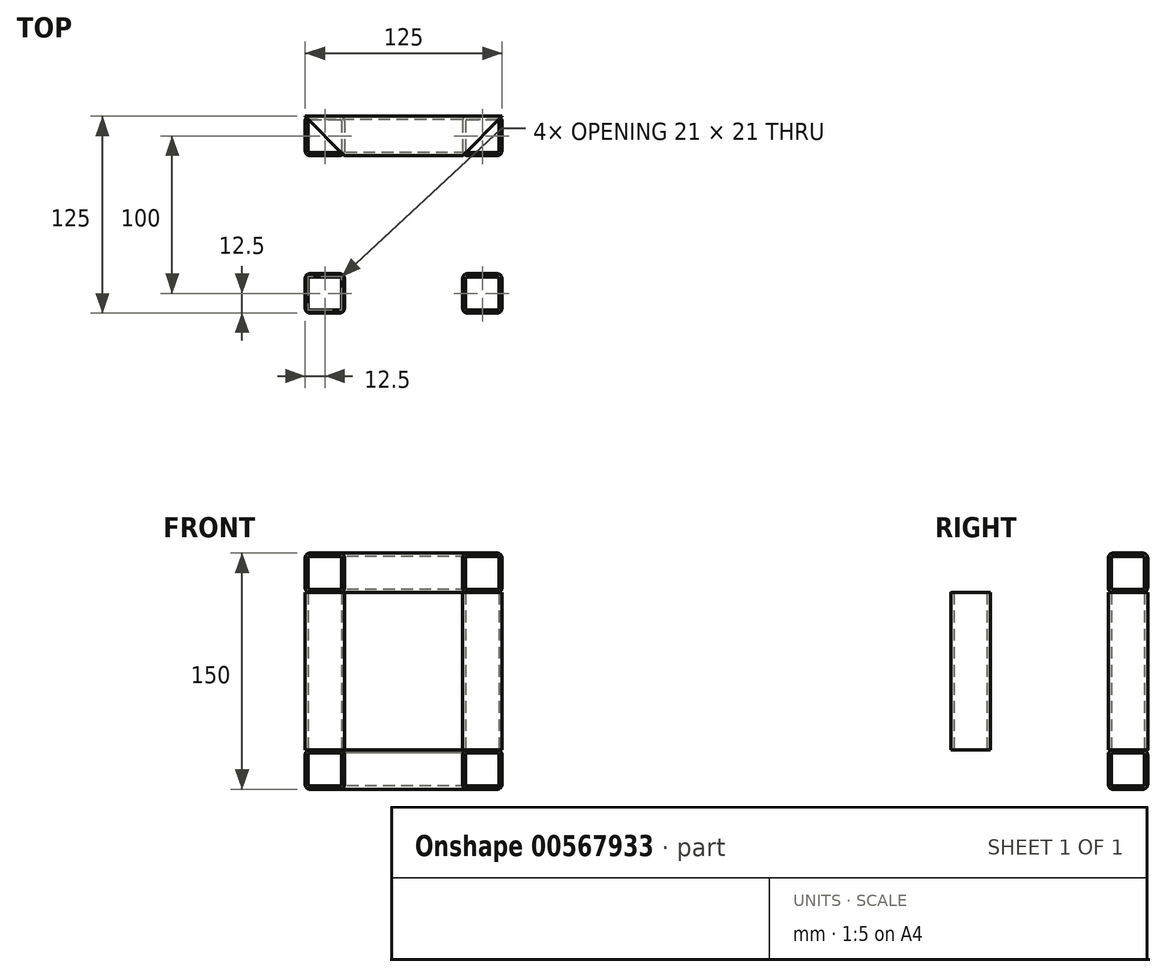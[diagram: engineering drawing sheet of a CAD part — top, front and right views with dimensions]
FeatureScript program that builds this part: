
annotation { "Feature Type Name" : "Feature", "Feature Type Description" : "" }
export const myFeature = defineFeature(function(context is Context, id is Id, definition is map)
    precondition{}
    {
        {
            var Q0;
            Q0=qCreatedBy(makeId("Top.planeOp"),FACE);
            var sketch = newSketch(context, id + "F0", { "sketchPlane" : qUnion([Q0])});
            skLineSegment(sketch, "E0.bottom", {"start": v(-59.5, 62.5) * mm, "end": v(-40.5, 62.5) * mm});
            skLineSegment(sketch, "E0.top", {"start": v(-59.5, 37.5) * mm, "end": v(-40.5, 37.5) * mm});
            skLineSegment(sketch, "E0.left", {"start": v(-62.5, 59.5) * mm, "end": v(-62.5, 40.5) * mm});
            skLineSegment(sketch, "E0.right", {"start": v(-37.5, 59.5) * mm, "end": v(-37.5, 40.5) * mm});
            skPoint(sketch, "E1.visualSharp", {"position": v(-62.5, 62.5) * mm});
            skArc(sketch, "E1.filletArc", {"start": v(-59.5, 62.5) * mm, "mid": v(-61.62, 61.62) * mm, "end": v(-62.5, 59.5) * mm});
            skPoint(sketch, "E2.visualSharp", {"position": v(-37.5, 62.5) * mm});
            skArc(sketch, "E2.filletArc", {"start": v(-37.5, 59.5) * mm, "mid": v(-38.38, 61.62) * mm, "end": v(-40.5, 62.5) * mm});
            skPoint(sketch, "E3.visualSharp", {"position": v(-37.5, 37.5) * mm});
            skArc(sketch, "E3.filletArc", {"start": v(-40.5, 37.5) * mm, "mid": v(-38.38, 38.38) * mm, "end": v(-37.5, 40.5) * mm});
            skPoint(sketch, "E4.visualSharp", {"position": v(-62.5, 37.5) * mm});
            skArc(sketch, "E4.filletArc", {"start": v(-62.5, 40.5) * mm, "mid": v(-61.62, 38.38) * mm, "end": v(-59.5, 37.5) * mm});
            skLineSegment(sketch, "E5.0", {"start": v(-59.5, 60.5) * mm, "end": v(-40.5, 60.5) * mm});
            skArc(sketch, "E5.1", {"start": v(-39.5, 59.5) * mm, "mid": v(-39.8, 60.2) * mm, "end": v(-40.5, 60.5) * mm});
            skArc(sketch, "E5.2", {"start": v(-59.5, 60.5) * mm, "mid": v(-60.2, 60.2) * mm, "end": v(-60.5, 59.5) * mm});
            skLineSegment(sketch, "E5.3", {"start": v(-39.5, 59.5) * mm, "end": v(-39.5, 40.5) * mm});
            skLineSegment(sketch, "E5.4", {"start": v(-60.5, 59.5) * mm, "end": v(-60.5, 40.5) * mm});
            skArc(sketch, "E5.5", {"start": v(-60.5, 40.5) * mm, "mid": v(-60.2, 39.8) * mm, "end": v(-59.5, 39.5) * mm});
            skLineSegment(sketch, "E5.6", {"start": v(-59.5, 39.5) * mm, "end": v(-40.5, 39.5) * mm});
            skArc(sketch, "E5.7", {"start": v(-40.5, 39.5) * mm, "mid": v(-39.8, 39.8) * mm, "end": v(-39.5, 40.5) * mm});
            skSolve(sketch);
        }
        {
            var Q0;
            Q0 = qSketchRegion(id + "F0", true);
            extrude(context, id + "F1", {"entities" : qUnion([Q0]), "depth" : 100 * mm, "offsetDistance" : 25 * mm});
        }
        {
            var Q0;
            Q0=makeQuery(id+"F1.opExtrude","SWEPT_BODY",BODY,{"disambiguationData":[OSD([sQuery(id+"F0.wireOp",EDGE,"E0.bottom"),sQuery(id+"F0.wireOp",EDGE,"E0.top"),sQuery(id+"F0.wireOp",EDGE,"E0.left"),sQuery(id+"F0.wireOp",EDGE,"E0.right"),sQuery(id+"F0.wireOp",EDGE,"E1.filletArc"),sQuery(id+"F0.wireOp",EDGE,"E2.filletArc"),sQuery(id+"F0.wireOp",EDGE,"E3.filletArc"),sQuery(id+"F0.wireOp",EDGE,"E4.filletArc"),sQuery(id+"F0.wireOp",EDGE,"E5.0"),sQuery(id+"F0.wireOp",EDGE,"E5.1"),sQuery(id+"F0.wireOp",EDGE,"E5.2"),sQuery(id+"F0.wireOp",EDGE,"E5.3"),sQuery(id+"F0.wireOp",EDGE,"E5.4"),sQuery(id+"F0.wireOp",EDGE,"E5.5"),sQuery(id+"F0.wireOp",EDGE,"E5.6"),sQuery(id+"F0.wireOp",EDGE,"E5.7")])]});
            transform(context, id + "F2", {"entities" : qUnion([Q0]), "transformType" : TransformType.TRANSLATION_3D, "dx" : 100 * mm, "dy" : 0 * mm, "dz" : 0 * mm, "makeCopy" : true});
        }
        {
            var Q0;
            Q0=makeQuery(id+"F1.opExtrude","SWEPT_BODY",BODY,{"disambiguationData":[OSD([sQuery(id+"F0.wireOp",EDGE,"E0.bottom"),sQuery(id+"F0.wireOp",EDGE,"E0.top"),sQuery(id+"F0.wireOp",EDGE,"E0.left"),sQuery(id+"F0.wireOp",EDGE,"E0.right"),sQuery(id+"F0.wireOp",EDGE,"E1.filletArc"),sQuery(id+"F0.wireOp",EDGE,"E2.filletArc"),sQuery(id+"F0.wireOp",EDGE,"E3.filletArc"),sQuery(id+"F0.wireOp",EDGE,"E4.filletArc"),sQuery(id+"F0.wireOp",EDGE,"E5.0"),sQuery(id+"F0.wireOp",EDGE,"E5.1"),sQuery(id+"F0.wireOp",EDGE,"E5.2"),sQuery(id+"F0.wireOp",EDGE,"E5.3"),sQuery(id+"F0.wireOp",EDGE,"E5.4"),sQuery(id+"F0.wireOp",EDGE,"E5.5"),sQuery(id+"F0.wireOp",EDGE,"E5.6"),sQuery(id+"F0.wireOp",EDGE,"E5.7")])]});
            transform(context, id + "F3", {"entities" : qUnion([Q0]), "transformType" : TransformType.TRANSLATION_3D, "dx" : 0 * mm, "dy" : -100 * mm, "dz" : 0 * mm, "makeCopy" : true});
        }
        {
            var Q0;
            Q0=makeQuery(id+"F3.opPattern","COPY",BODY,{"derivedFrom":makeQuery(id+"F1.opExtrude","SWEPT_BODY",BODY,{"disambiguationData":[OSD([sQuery(id+"F0.wireOp",EDGE,"E0.bottom"),sQuery(id+"F0.wireOp",EDGE,"E0.top"),sQuery(id+"F0.wireOp",EDGE,"E0.left"),sQuery(id+"F0.wireOp",EDGE,"E0.right"),sQuery(id+"F0.wireOp",EDGE,"E1.filletArc"),sQuery(id+"F0.wireOp",EDGE,"E2.filletArc"),sQuery(id+"F0.wireOp",EDGE,"E3.filletArc"),sQuery(id+"F0.wireOp",EDGE,"E4.filletArc"),sQuery(id+"F0.wireOp",EDGE,"E5.0"),sQuery(id+"F0.wireOp",EDGE,"E5.1"),sQuery(id+"F0.wireOp",EDGE,"E5.2"),sQuery(id+"F0.wireOp",EDGE,"E5.3"),sQuery(id+"F0.wireOp",EDGE,"E5.4"),sQuery(id+"F0.wireOp",EDGE,"E5.5"),sQuery(id+"F0.wireOp",EDGE,"E5.6"),sQuery(id+"F0.wireOp",EDGE,"E5.7")])]}),"instanceName":"1"});
            transform(context, id + "F4", {"entities" : qUnion([Q0]), "transformType" : TransformType.TRANSLATION_3D, "dx" : 100 * mm, "dy" : 0 * mm, "dz" : 0 * mm, "makeCopy" : true});
        }
        {
            var Q0;
            Q0=qCreatedBy(makeId("Right.planeOp"),FACE);
            var sketch = newSketch(context, id + "F5", { "sketchPlane" : qUnion([Q0])});
            skLineSegment(sketch, "E6.bottom", {"start": v(40.5, 125) * mm, "end": v(59.5, 125) * mm});
            skLineSegment(sketch, "E6.top", {"start": v(40.5, 100) * mm, "end": v(59.5, 100) * mm});
            skLineSegment(sketch, "E6.left", {"start": v(37.5, 122) * mm, "end": v(37.5, 103) * mm});
            skLineSegment(sketch, "E6.right", {"start": v(62.5, 122) * mm, "end": v(62.5, 103) * mm});
            skPoint(sketch, "E6.middle", {"position": v(50, 112.5) * mm});
            skPoint(sketch, "E7.visualSharp", {"position": v(62.5, 125) * mm});
            skArc(sketch, "E7.filletArc", {"start": v(62.5, 122) * mm, "mid": v(61.62, 124.12) * mm, "end": v(59.5, 125) * mm});
            skPoint(sketch, "E8.visualSharp", {"position": v(37.5, 125) * mm});
            skArc(sketch, "E8.filletArc", {"start": v(40.5, 125) * mm, "mid": v(38.38, 124.12) * mm, "end": v(37.5, 122) * mm});
            skPoint(sketch, "E9.visualSharp", {"position": v(37.5, 100) * mm});
            skArc(sketch, "E9.filletArc", {"start": v(37.5, 103) * mm, "mid": v(38.38, 100.88) * mm, "end": v(40.5, 100) * mm});
            skPoint(sketch, "E10.visualSharp", {"position": v(62.5, 100) * mm});
            skArc(sketch, "E10.filletArc", {"start": v(59.5, 100) * mm, "mid": v(61.62, 100.88) * mm, "end": v(62.5, 103) * mm});
            skArc(sketch, "E11.0", {"start": v(39.5, 103) * mm, "mid": v(39.8, 102.3) * mm, "end": v(40.5, 102) * mm});
            skLineSegment(sketch, "E11.1", {"start": v(39.5, 122) * mm, "end": v(39.5, 103) * mm});
            skLineSegment(sketch, "E11.2", {"start": v(40.5, 102) * mm, "end": v(59.5, 102) * mm});
            skArc(sketch, "E11.3", {"start": v(40.5, 123) * mm, "mid": v(39.8, 122.7) * mm, "end": v(39.5, 122) * mm});
            skArc(sketch, "E11.4", {"start": v(59.5, 102) * mm, "mid": v(60.2, 102.3) * mm, "end": v(60.5, 103) * mm});
            skLineSegment(sketch, "E11.5", {"start": v(60.5, 122) * mm, "end": v(60.5, 103) * mm});
            skArc(sketch, "E11.6", {"start": v(60.5, 122) * mm, "mid": v(60.2, 122.7) * mm, "end": v(59.5, 123) * mm});
            skLineSegment(sketch, "E11.7", {"start": v(40.5, 123) * mm, "end": v(59.5, 123) * mm});
            skSolve(sketch);
        }
        {
            var Q0;
            Q0 = qSketchRegion(id + "F5", true);
            extrude(context, id + "F6", {"entities" : qUnion([Q0]), "endBound" : BoundingType.SYMMETRIC, "depth" : 150 * mm, "offsetDistance" : 25 * mm});
        }
        {
            var Q0;
            Q0=makeQuery(id+"F6.opExtrude","SWEPT_FACE",FACE,{"disambiguationData":[OSD([sQuery(id+"F5.wireOp",EDGE,"E6.bottom")])]});
            var sketch = newSketch(context, id + "F7", { "sketchPlane" : qUnion([Q0])});
            skLineSegment(sketch, "E12", {"start": v(0, 0) * mm, "end": v(-102.25, 102.25) * mm});
            skLineSegment(sketch, "E13", {"start": v(-102.25, 102.25) * mm, "end": v(-102.25, 0) * mm});
            skLineSegment(sketch, "E14", {"start": v(-102.25, 0) * mm, "end": v(0, 0) * mm});
            skSolve(sketch);
        }
        {
            var Q0;
            Q0 = qSketchRegion(id + "F7", true);
            extrude(context, id + "F8", {"entities" : qUnion([Q0]), "operationType" : NewBodyOperationType.REMOVE, "oppositeDirection" : true, "depth" : 25 * mm, "offsetDistance" : 25 * mm});
        }
        {
            var Q0;
            Q0=makeQuery(id+"F6.opExtrude","SWEPT_FACE",FACE,{"disambiguationData":[OSD([sQuery(id+"F5.wireOp",EDGE,"E6.bottom")])]});
            var sketch = newSketch(context, id + "F9", { "sketchPlane" : qUnion([Q0])});
            skLineSegment(sketch, "E15", {"start": v(0, 0) * mm, "end": v(99.52, 99.52) * mm});
            skLineSegment(sketch, "E16", {"start": v(99.52, 99.52) * mm, "end": v(99.52, 0) * mm});
            skLineSegment(sketch, "E17", {"start": v(99.52, 0) * mm, "end": v(0, 0) * mm});
            skSolve(sketch);
        }
        {
            var Q0;
            Q0 = qSketchRegion(id + "F9", true);
            extrude(context, id + "F10", {"entities" : qUnion([Q0]), "operationType" : NewBodyOperationType.REMOVE, "oppositeDirection" : true, "depth" : 25 * mm, "offsetDistance" : 25 * mm});
        }
        {
            var Q0;
            Q0=makeQuery(id+"F6.opExtrude","SWEPT_BODY",BODY,{"disambiguationData":[OSD([sQuery(id+"F5.wireOp",EDGE,"E6.bottom"),sQuery(id+"F5.wireOp",EDGE,"E6.top"),sQuery(id+"F5.wireOp",EDGE,"E6.left"),sQuery(id+"F5.wireOp",EDGE,"E6.right"),sQuery(id+"F5.wireOp",EDGE,"E7.filletArc"),sQuery(id+"F5.wireOp",EDGE,"E8.filletArc"),sQuery(id+"F5.wireOp",EDGE,"E9.filletArc"),sQuery(id+"F5.wireOp",EDGE,"E10.filletArc"),sQuery(id+"F5.wireOp",EDGE,"E11.0"),sQuery(id+"F5.wireOp",EDGE,"E11.1"),sQuery(id+"F5.wireOp",EDGE,"E11.2"),sQuery(id+"F5.wireOp",EDGE,"E11.3"),sQuery(id+"F5.wireOp",EDGE,"E11.4"),sQuery(id+"F5.wireOp",EDGE,"E11.5"),sQuery(id+"F5.wireOp",EDGE,"E11.6"),sQuery(id+"F5.wireOp",EDGE,"E11.7")])]});
            transform(context, id + "F11", {"entities" : qUnion([Q0]), "transformType" : TransformType.TRANSLATION_3D, "dx" : 0 * mm, "dy" : 0 * mm, "dz" : -125 * mm, "makeCopy" : true});
        }
    });
